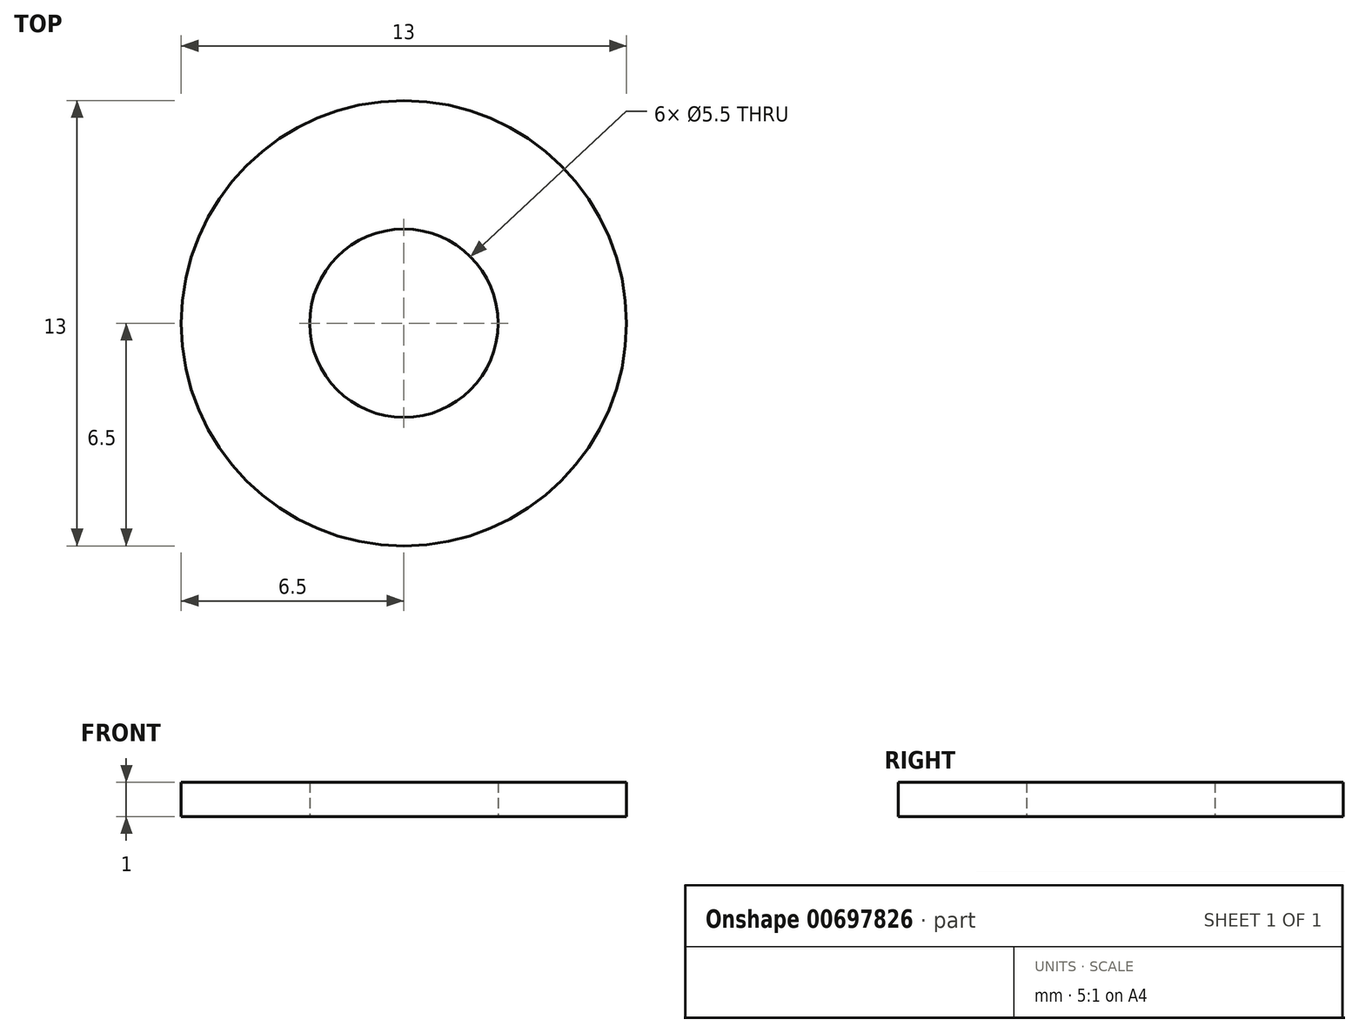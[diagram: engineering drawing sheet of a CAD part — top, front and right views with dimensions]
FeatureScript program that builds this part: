
annotation { "Feature Type Name" : "Feature", "Feature Type Description" : "" }
export const myFeature = defineFeature(function(context is Context, id is Id, definition is map)
    precondition{}
    {
        {
            var Q0;
            Q0=qCreatedBy(makeId("Top.planeOp"),FACE);
            var sketch = newSketch(context, id + "F0", { "sketchPlane" : qUnion([Q0])});
            skCircle(sketch, "E0", {"center": v(0, 0) * mm, "radius": 2.75 * mm});
            skCircle(sketch, "E1", {"center": v(0, 0) * mm, "radius": 6.5 * mm});
            skSolve(sketch);
        }
        {
            var Q0;
            Q0 = qSketchRegion(id + "F0", true);
            extrude(context, id + "F1", {"entities" : qUnion([Q0]), "depth" : 1 * mm, "offsetDistance" : 25 * mm});
        }
    });
